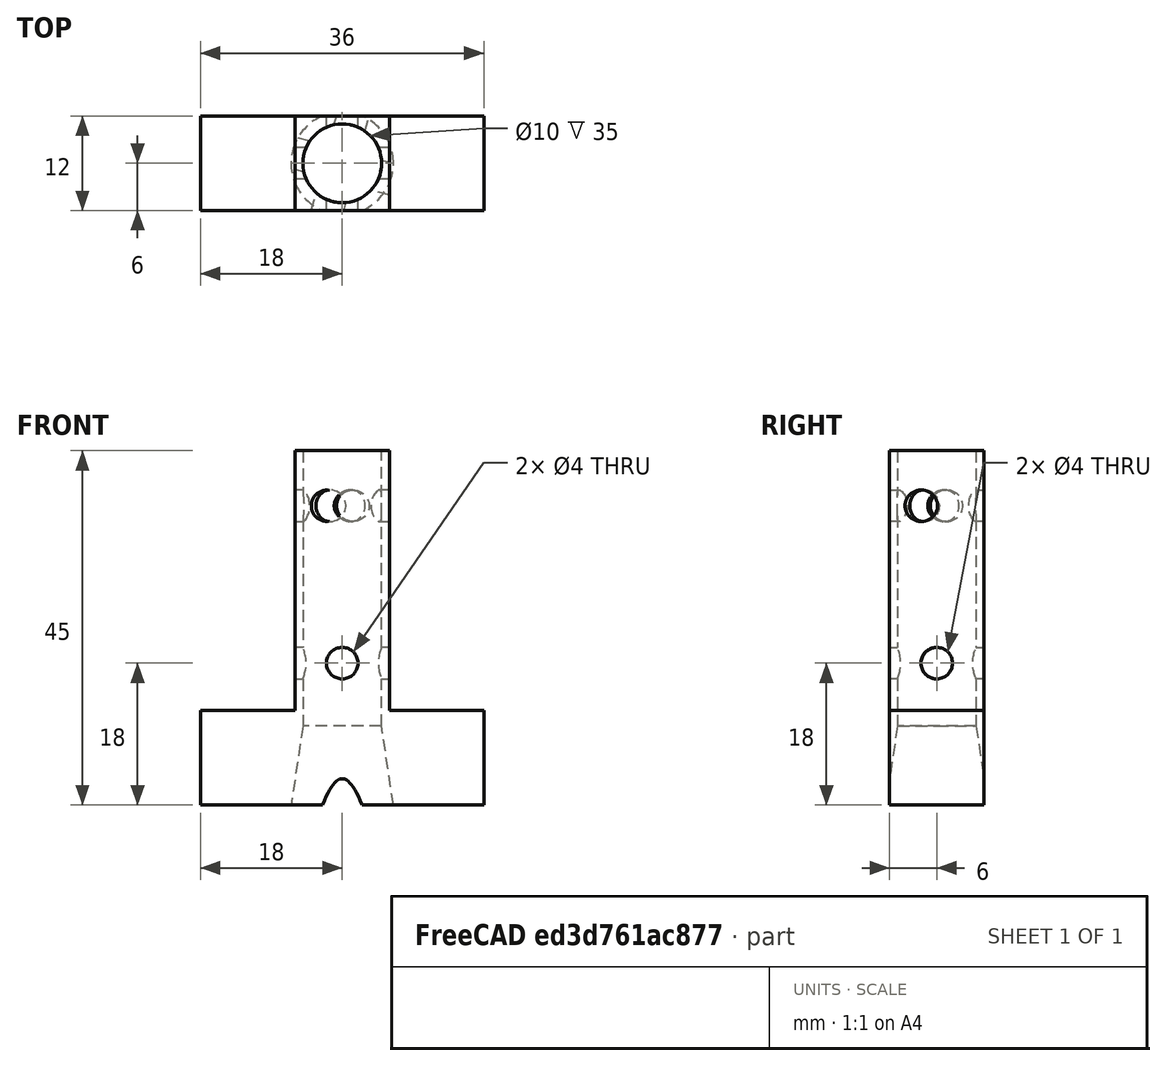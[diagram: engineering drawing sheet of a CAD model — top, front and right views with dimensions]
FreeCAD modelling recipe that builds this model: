
FCSTD DOCUMENT  (FreeCAD 0.20R29410 (Git))
Label: barrel0
License: All rights reserved
LicenseURL: http://en.wikipedia.org/wiki/All_rights_reserved
objects: Part::Cylinder×7, Part::MultiFuse×6, Part::Cut×5, Part::Box×4, Part::Cone×1, Part::Feature×1
note: 24 computed .brp shape members not serialized (recipe doc carries the construction recipe); baked Part::Feature solids carry a one-line shape summary decoded from their .brp

FEATURE [Part::Box] Box  label="Cube"
  AttacherType = Attacher::AttachEngine3D
  Height = 45
  Length = 12
  Width = 12
FEATURE [Part::Cylinder] Cylinder
  Angle = 360
  AttacherType = Attacher::AttachEngine3D
  FirstAngle = 0
  Height = 54
  Placement = pos=(6,6,-5.75) rot=(0,0,1;0rad)
  Radius = 5
  SecondAngle = 0
FEATURE [Part::Cylinder] Cylinder001
  Angle = 360
  AttacherType = Attacher::AttachEngine3D
  FirstAngle = 0
  Height = 4
  Placement = pos=(0,-10.5,0) rot=(0,0,1;0rad)
  Radius = 5
  SecondAngle = 0
FEATURE [Part::Cylinder] Cylinder002
  Angle = 360
  AttacherType = Attacher::AttachEngine3D
  FirstAngle = 0
  Height = 4
  Placement = pos=(0,-10.5,0) rot=(0,0,1;0rad)
  Radius = 2
  SecondAngle = 0
FEATURE [Part::Cut] Cut001
  Base = -> Cylinder001
  Placement = pos=(6,16.5,0) rot=(0,0,1;0rad)
  Tool = -> Cylinder002
FEATURE [Part::Cut] Cut
  Base = -> Box
  Tool = -> Cylinder
FEATURE [Part::MultiFuse] Fusion
  Shapes = -> [Cut001,Cut]
FEATURE [Part::Box] Box001  label="Cube001"
  AttacherType = Attacher::AttachEngine3D
  Height = 12
  Length = 12
  Placement = pos=(-12,0,0) rot=(0,0,1;0rad)
  Width = 12
FEATURE [Part::Box] Box002  label="Cube002"
  AttacherType = Attacher::AttachEngine3D
  Height = 12
  Length = 12
  Placement = pos=(12,0,0) rot=(0,0,1;0rad)
  Width = 12
FEATURE [Part::MultiFuse] Fusion001
  Shapes = -> [Box002,Fusion]
FEATURE [Part::MultiFuse] Fusion002
  Shapes = -> [Fusion001,Box001]
FEATURE [Part::Cone] Cone
  Angle = 360
  AttacherType = Attacher::AttachEngine3D
  Height = 10
  Placement = pos=(6,6,0) rot=(0,0,1;0rad)
  Radius1 = 6.5
  Radius2 = 5
FEATURE [Part::Cut] Cut002
  Base = -> Fusion002
  Tool = -> Cone
FEATURE [Part::Box] Box003  label="Cube003"
  AttacherType = Attacher::AttachEngine3D
  Height = 12
  Length = 36
  Placement = pos=(-12,-2,0) rot=(0,0,1;0rad)
  Width = 2
FEATURE [Part::Cylinder] Cylinder003
  Angle = 360
  AttacherType = Attacher::AttachEngine3D
  FirstAngle = 0
  Height = 20
  Placement = pos=(-4,6,47) rot=(0,1,0;1.5708rad)
  Radius = 2
  SecondAngle = 0
FEATURE [Part::Cylinder] Cylinder004
  Angle = 360
  AttacherType = Attacher::AttachEngine3D
  FirstAngle = 0
  Height = 20
  Placement = pos=(6,15,47) rot=(0.57735,0.57735,-0.57735;2.0944rad)
  Radius = 2
  SecondAngle = 0
FEATURE [Part::MultiFuse] Fusion003
  Placement = pos=(0,0,-29) rot=(0,0,1;0rad)
  Shapes = -> [Cylinder003,Cylinder004]
FEATURE [Part::Cylinder] Cylinder005
  Angle = 360
  AttacherType = Attacher::AttachEngine3D
  FirstAngle = 0
  Height = 20
  Placement = pos=(-4,6,47) rot=(0,1,0;1.5708rad)
  Radius = 2
  SecondAngle = 0
FEATURE [Part::Cylinder] Cylinder006
  Angle = 360
  AttacherType = Attacher::AttachEngine3D
  FirstAngle = 0
  Height = 20
  Placement = pos=(6,15,47) rot=(0.57735,0.57735,-0.57735;2.0944rad)
  Radius = 2
  SecondAngle = 0
FEATURE [Part::MultiFuse] Fusion004
  Placement = pos=(-1.67303,1.48356,-9) rot=(0,0,-1;0.261799rad)
  Shapes = -> [Cylinder005,Cylinder006]
FEATURE [Part::MultiFuse] Fusion005
  Shapes = -> [Fusion004,Fusion003]
FEATURE [Part::Cut] Cut003
  Base = -> Cut002
  Tool = -> Fusion005
FEATURE [Part::Cut] Cut004
  Base = -> Cut003
  Tool = -> Box003
FEATURE [Part::Feature] Cut004_solid  label="Cut004 (Solid)"
  shape: bbox 36 x 14.28 x 45 mm, 30 faces (baked)
